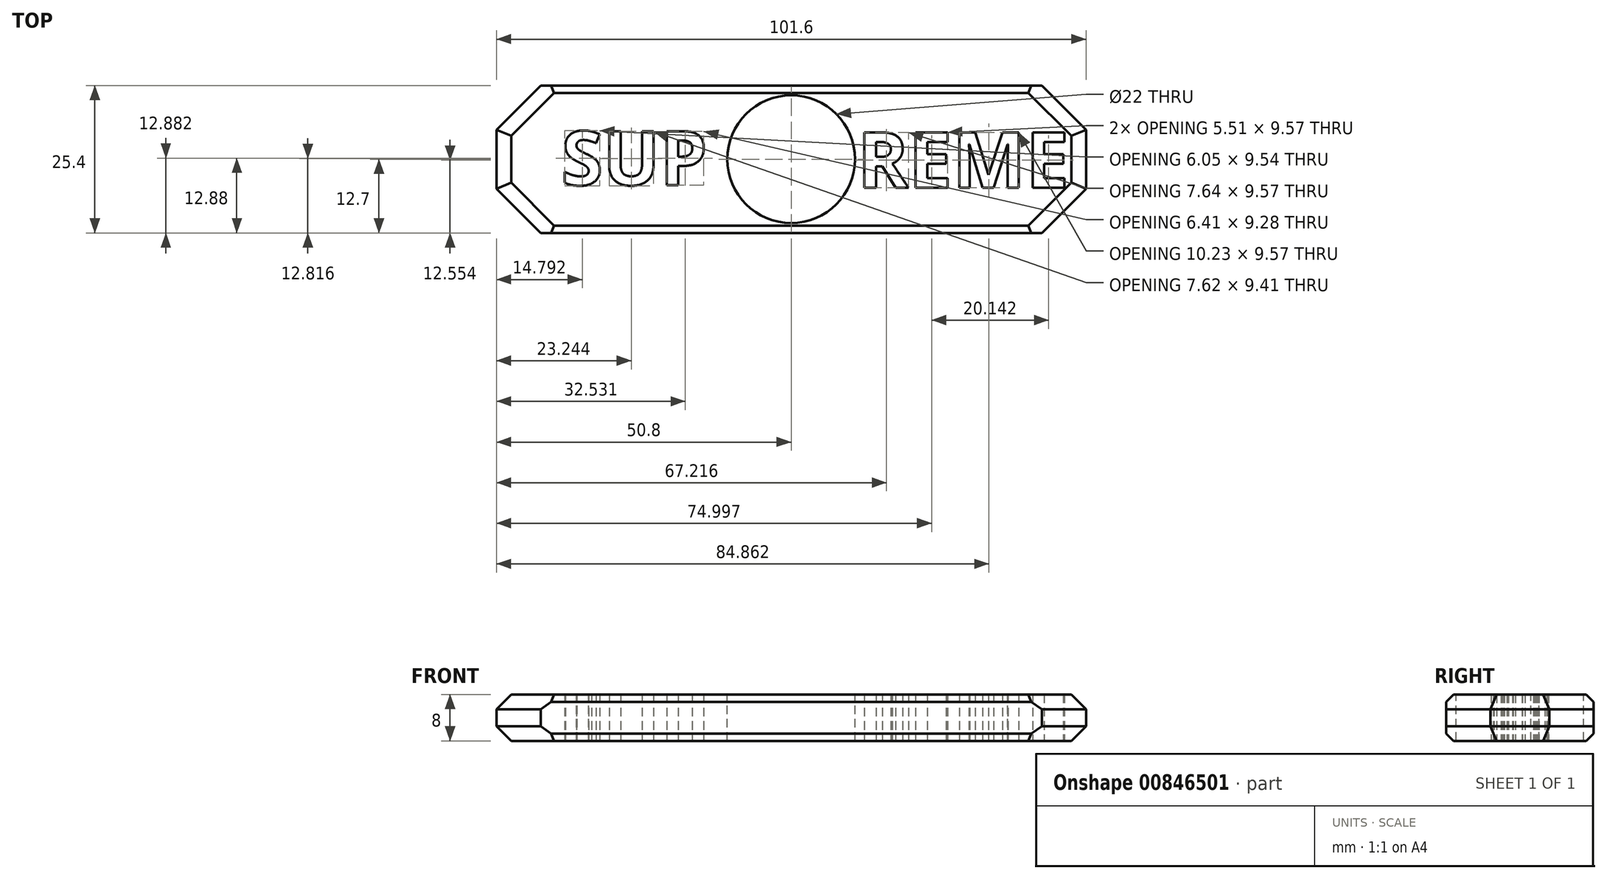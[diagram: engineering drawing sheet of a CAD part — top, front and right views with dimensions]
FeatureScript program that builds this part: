
annotation { "Feature Type Name" : "Feature", "Feature Type Description" : "" }
export const myFeature = defineFeature(function(context is Context, id is Id, definition is map)
    precondition{}
    {
        {
            var Q0;
            Q0=qCreatedBy(makeId("Top.planeOp"),FACE);
            var sketch = newSketch(context, id + "F0", { "sketchPlane" : qUnion([Q0])});
            skLineSegment(sketch, "E0.bottom", {"start": v(-50.8, -12.7) * mm, "end": v(50.8, -12.7) * mm});
            skLineSegment(sketch, "E0.top", {"start": v(-50.8, 12.7) * mm, "end": v(50.8, 12.7) * mm});
            skLineSegment(sketch, "E0.left", {"start": v(-50.8, -12.7) * mm, "end": v(-50.8, 12.7) * mm});
            skLineSegment(sketch, "E0.right", {"start": v(50.8, -12.7) * mm, "end": v(50.8, 12.7) * mm});
            skPoint(sketch, "E0.middle", {"position": v(0, 0) * mm});
            skSolve(sketch);
        }
        {
            var Q0;
            Q0 = qSketchRegion(id + "F0", true);
            extrude(context, id + "F1", {"entities" : qUnion([Q0]), "depth" : 8 * mm, "offsetDistance" : 25.4 * mm});
        }
        {
            var Q0;
            Q0=qCreatedBy(makeId("Top.planeOp"),FACE);
            var sketch = newSketch(context, id + "F2", { "sketchPlane" : qUnion([Q0])});
            skCircle(sketch, "E1", {"center": v(0, 0) * mm, "radius": 11 * mm});
            skSolve(sketch);
        }
        {
            var Q0;
            Q0 = qSketchRegion(id + "F2", true);
            extrude(context, id + "F3", {"entities" : qUnion([Q0]), "operationType" : NewBodyOperationType.REMOVE, "oppositeDirection" : true, "depth" : 25.4 * mm, "offsetDistance" : 25.4 * mm, "hasSecondDirection" : true, "secondDirectionOppositeDirection" : false, "secondDirectionDepth" : 25.4 * mm});
        }
        {
            var Q0;
            Q0=qCreatedBy(makeId("Top.planeOp"),FACE);
            var sketch = newSketch(context, id + "F4", { "sketchPlane" : qUnion([Q0])});
            skText(sketch, "E2", { "text": "SUP\n", "fontName": "OpenSans-Bold.ttf"});
            skText(sketch, "E3", { "text": "REME\n", "fontName": "OpenSans-Bold.ttf"});
            const initialGuessF4  = {"E2": [-0.03963, -0.00446, 1, 0, 0.00936], "E3": [0.01139, -0.00493, 1, 0, 0.00965]};
            skSetInitialGuess(sketch, initialGuessF4);
            skSolve(sketch);
        }
        {
            var Q0;
            Q0 = qSketchRegion(id + "F4", true);
            extrude(context, id + "F5", {"entities" : qUnion([Q0]), "operationType" : NewBodyOperationType.REMOVE, "depth" : 70.36 * mm, "offsetDistance" : 25.4 * mm});
        }
        {
            var Q0;
            Q0=makeQuery(id+"F1.opExtrude","SWEPT_EDGE",EDGE,{"disambiguationData":[OSD([sQuery(id+"F0.wireOp",EDGE,"E0.top"),sQuery(id+"F0.wireOp",EDGE,"E0.left")])]});
            var Q1;
            Q1=makeQuery(id+"F1.opExtrude","SWEPT_EDGE",EDGE,{"disambiguationData":[OSD([sQuery(id+"F0.wireOp",EDGE,"E0.bottom"),sQuery(id+"F0.wireOp",EDGE,"E0.left")])]});
            var Q2;
            Q2=makeQuery(id+"F1.opExtrude","SWEPT_EDGE",EDGE,{"disambiguationData":[OSD([sQuery(id+"F0.wireOp",EDGE,"E0.bottom"),sQuery(id+"F0.wireOp",EDGE,"E0.right")])]});
            var Q3;
            Q3=makeQuery(id+"F1.opExtrude","SWEPT_EDGE",EDGE,{"disambiguationData":[OSD([sQuery(id+"F0.wireOp",EDGE,"E0.top"),sQuery(id+"F0.wireOp",EDGE,"E0.right")])]});
            chamfer(context, id + "F6", {"entities" : qUnion([Q0, Q1, Q2, Q3]), "width" : 7.62 * mm, "tangentPropagation" : true});
        }
        {
            var Q0;
            Q0=makeQuery(id+"F1.opExtrude","CAP_EDGE",EDGE,{"disambiguationData":[OSD([sQuery(id+"F0.wireOp",EDGE,"E0.bottom")])],"isStart":false});
            var Q1;
            Q1=makeQuery(id+"F1.opExtrude","CAP_EDGE",EDGE,{"disambiguationData":[OSD([sQuery(id+"F0.wireOp",EDGE,"E0.top")])],"isStart":false});
            var Q2;
            Q2=makeQuery(id+"F1.opExtrude","CAP_EDGE",EDGE,{"disambiguationData":[OSD([sQuery(id+"F0.wireOp",EDGE,"E0.bottom")])],"isStart":true});
            var Q3;
            Q3=makeQuery(id+"F1.opExtrude","CAP_EDGE",EDGE,{"disambiguationData":[OSD([sQuery(id+"F0.wireOp",EDGE,"E0.top")])],"isStart":true});
            chamfer(context, id + "F7", {"entities" : qUnion([Q0, Q1, Q2, Q3]), "width" : 1.27 * mm, "tangentPropagation" : true});
        }
        {
            var Q0;
            {var subQ0=sQuery(id+"F0.wireOp",EDGE,"E0.right");var subQ1=sQuery(id+"F0.wireOp",EDGE,"E0.left");var subQ2=sQuery(id+"F0.wireOp",EDGE,"E0.top");var subQ3=sQuery(id+"F0.wireOp",EDGE,"E0.bottom");Q0=makeQuery(id+"F6.opChamfer","BLEND_EDGE",EDGE,{"blendedFrom":[makeQuery(id+"F1.opExtrude","SWEPT_EDGE",EDGE,{"disambiguationData":[OSD([subQ3,subQ1])]}),makeQuery(id+"F5.boolean.opBoolean","SPLIT",FACE,{"disambiguationData":[TD([makeQuery(id+"F1.opExtrude","SWEPT_FACE",FACE,{"disambiguationData":[OSD([subQ3])]})])],"derivedFrom":makeQuery(id+"F1.opExtrude","CAP_FACE",FACE,{"disambiguationData":[OSD([subQ3,subQ2,subQ1,subQ0])],"isStart":true})})],"blendedInto":[makeQuery(id+"F5.boolean.opBoolean","SPLIT",FACE,{"disambiguationData":[TD([makeQuery(id+"F1.opExtrude","SWEPT_FACE",FACE,{"disambiguationData":[OSD([subQ3])]})])],"derivedFrom":makeQuery(id+"F1.opExtrude","CAP_FACE",FACE,{"disambiguationData":[OSD([subQ3,subQ2,subQ1,subQ0])],"isStart":true})})]});}
            var Q1;
            Q1=makeQuery(id+"F1.opExtrude","CAP_EDGE",EDGE,{"disambiguationData":[OSD([sQuery(id+"F0.wireOp",EDGE,"E0.left")])],"isStart":true});
            var Q2;
            {var subQ0=sQuery(id+"F0.wireOp",EDGE,"E0.right");var subQ1=sQuery(id+"F0.wireOp",EDGE,"E0.left");var subQ2=sQuery(id+"F0.wireOp",EDGE,"E0.top");var subQ3=sQuery(id+"F0.wireOp",EDGE,"E0.bottom");Q2=makeQuery(id+"F6.opChamfer","BLEND_EDGE",EDGE,{"blendedFrom":[makeQuery(id+"F1.opExtrude","SWEPT_EDGE",EDGE,{"disambiguationData":[OSD([subQ3,subQ1])]}),makeQuery(id+"F5.boolean.opBoolean","SPLIT",FACE,{"disambiguationData":[TD([makeQuery(id+"F1.opExtrude","SWEPT_FACE",FACE,{"disambiguationData":[OSD([subQ3])]})])],"derivedFrom":makeQuery(id+"F1.opExtrude","CAP_FACE",FACE,{"disambiguationData":[OSD([subQ3,subQ2,subQ1,subQ0])],"isStart":false})})],"blendedInto":[makeQuery(id+"F5.boolean.opBoolean","SPLIT",FACE,{"disambiguationData":[TD([makeQuery(id+"F1.opExtrude","SWEPT_FACE",FACE,{"disambiguationData":[OSD([subQ3])]})])],"derivedFrom":makeQuery(id+"F1.opExtrude","CAP_FACE",FACE,{"disambiguationData":[OSD([subQ3,subQ2,subQ1,subQ0])],"isStart":false})})]});}
            var Q3;
            Q3=makeQuery(id+"F1.opExtrude","CAP_EDGE",EDGE,{"disambiguationData":[OSD([sQuery(id+"F0.wireOp",EDGE,"E0.left")])],"isStart":false});
            var Q4;
            {var subQ0=sQuery(id+"F0.wireOp",EDGE,"E0.right");var subQ1=sQuery(id+"F0.wireOp",EDGE,"E0.left");var subQ2=sQuery(id+"F0.wireOp",EDGE,"E0.top");var subQ3=sQuery(id+"F0.wireOp",EDGE,"E0.bottom");Q4=makeQuery(id+"F6.opChamfer","BLEND_EDGE",EDGE,{"blendedFrom":[makeQuery(id+"F1.opExtrude","SWEPT_EDGE",EDGE,{"disambiguationData":[OSD([subQ2,subQ1])]}),makeQuery(id+"F5.boolean.opBoolean","SPLIT",FACE,{"disambiguationData":[TD([makeQuery(id+"F1.opExtrude","SWEPT_FACE",FACE,{"disambiguationData":[OSD([subQ3])]})])],"derivedFrom":makeQuery(id+"F1.opExtrude","CAP_FACE",FACE,{"disambiguationData":[OSD([subQ3,subQ2,subQ1,subQ0])],"isStart":false})})],"blendedInto":[makeQuery(id+"F5.boolean.opBoolean","SPLIT",FACE,{"disambiguationData":[TD([makeQuery(id+"F1.opExtrude","SWEPT_FACE",FACE,{"disambiguationData":[OSD([subQ3])]})])],"derivedFrom":makeQuery(id+"F1.opExtrude","CAP_FACE",FACE,{"disambiguationData":[OSD([subQ3,subQ2,subQ1,subQ0])],"isStart":false})})]});}
            var Q5;
            {var subQ0=sQuery(id+"F0.wireOp",EDGE,"E0.right");var subQ1=sQuery(id+"F0.wireOp",EDGE,"E0.left");var subQ2=sQuery(id+"F0.wireOp",EDGE,"E0.top");var subQ3=sQuery(id+"F0.wireOp",EDGE,"E0.bottom");Q5=makeQuery(id+"F6.opChamfer","BLEND_EDGE",EDGE,{"blendedFrom":[makeQuery(id+"F1.opExtrude","SWEPT_EDGE",EDGE,{"disambiguationData":[OSD([subQ2,subQ1])]}),makeQuery(id+"F5.boolean.opBoolean","SPLIT",FACE,{"disambiguationData":[TD([makeQuery(id+"F1.opExtrude","SWEPT_FACE",FACE,{"disambiguationData":[OSD([subQ3])]})])],"derivedFrom":makeQuery(id+"F1.opExtrude","CAP_FACE",FACE,{"disambiguationData":[OSD([subQ3,subQ2,subQ1,subQ0])],"isStart":true})})],"blendedInto":[makeQuery(id+"F5.boolean.opBoolean","SPLIT",FACE,{"disambiguationData":[TD([makeQuery(id+"F1.opExtrude","SWEPT_FACE",FACE,{"disambiguationData":[OSD([subQ3])]})])],"derivedFrom":makeQuery(id+"F1.opExtrude","CAP_FACE",FACE,{"disambiguationData":[OSD([subQ3,subQ2,subQ1,subQ0])],"isStart":true})})]});}
            var Q6;
            {var subQ0=sQuery(id+"F0.wireOp",EDGE,"E0.right");var subQ1=sQuery(id+"F0.wireOp",EDGE,"E0.left");var subQ2=sQuery(id+"F0.wireOp",EDGE,"E0.top");var subQ3=sQuery(id+"F0.wireOp",EDGE,"E0.bottom");Q6=makeQuery(id+"F6.opChamfer","BLEND_EDGE",EDGE,{"blendedFrom":[makeQuery(id+"F1.opExtrude","SWEPT_EDGE",EDGE,{"disambiguationData":[OSD([subQ2,subQ0])]}),makeQuery(id+"F5.boolean.opBoolean","SPLIT",FACE,{"disambiguationData":[TD([makeQuery(id+"F1.opExtrude","SWEPT_FACE",FACE,{"disambiguationData":[OSD([subQ3])]})])],"derivedFrom":makeQuery(id+"F1.opExtrude","CAP_FACE",FACE,{"disambiguationData":[OSD([subQ3,subQ2,subQ1,subQ0])],"isStart":false})})],"blendedInto":[makeQuery(id+"F5.boolean.opBoolean","SPLIT",FACE,{"disambiguationData":[TD([makeQuery(id+"F1.opExtrude","SWEPT_FACE",FACE,{"disambiguationData":[OSD([subQ3])]})])],"derivedFrom":makeQuery(id+"F1.opExtrude","CAP_FACE",FACE,{"disambiguationData":[OSD([subQ3,subQ2,subQ1,subQ0])],"isStart":false})})]});}
            var Q7;
            Q7=makeQuery(id+"F1.opExtrude","CAP_EDGE",EDGE,{"disambiguationData":[OSD([sQuery(id+"F0.wireOp",EDGE,"E0.right")])],"isStart":false});
            var Q8;
            {var subQ0=sQuery(id+"F0.wireOp",EDGE,"E0.right");var subQ1=sQuery(id+"F0.wireOp",EDGE,"E0.left");var subQ2=sQuery(id+"F0.wireOp",EDGE,"E0.top");var subQ3=sQuery(id+"F0.wireOp",EDGE,"E0.bottom");Q8=makeQuery(id+"F6.opChamfer","BLEND_EDGE",EDGE,{"blendedFrom":[makeQuery(id+"F1.opExtrude","SWEPT_EDGE",EDGE,{"disambiguationData":[OSD([subQ3,subQ0])]}),makeQuery(id+"F5.boolean.opBoolean","SPLIT",FACE,{"disambiguationData":[TD([makeQuery(id+"F1.opExtrude","SWEPT_FACE",FACE,{"disambiguationData":[OSD([subQ3])]})])],"derivedFrom":makeQuery(id+"F1.opExtrude","CAP_FACE",FACE,{"disambiguationData":[OSD([subQ3,subQ2,subQ1,subQ0])],"isStart":false})})],"blendedInto":[makeQuery(id+"F5.boolean.opBoolean","SPLIT",FACE,{"disambiguationData":[TD([makeQuery(id+"F1.opExtrude","SWEPT_FACE",FACE,{"disambiguationData":[OSD([subQ3])]})])],"derivedFrom":makeQuery(id+"F1.opExtrude","CAP_FACE",FACE,{"disambiguationData":[OSD([subQ3,subQ2,subQ1,subQ0])],"isStart":false})})]});}
            var Q9;
            {var subQ0=sQuery(id+"F0.wireOp",EDGE,"E0.right");var subQ1=sQuery(id+"F0.wireOp",EDGE,"E0.left");var subQ2=sQuery(id+"F0.wireOp",EDGE,"E0.top");var subQ3=sQuery(id+"F0.wireOp",EDGE,"E0.bottom");Q9=makeQuery(id+"F6.opChamfer","BLEND_EDGE",EDGE,{"blendedFrom":[makeQuery(id+"F1.opExtrude","SWEPT_EDGE",EDGE,{"disambiguationData":[OSD([subQ3,subQ0])]}),makeQuery(id+"F5.boolean.opBoolean","SPLIT",FACE,{"disambiguationData":[TD([makeQuery(id+"F1.opExtrude","SWEPT_FACE",FACE,{"disambiguationData":[OSD([subQ3])]})])],"derivedFrom":makeQuery(id+"F1.opExtrude","CAP_FACE",FACE,{"disambiguationData":[OSD([subQ3,subQ2,subQ1,subQ0])],"isStart":true})})],"blendedInto":[makeQuery(id+"F5.boolean.opBoolean","SPLIT",FACE,{"disambiguationData":[TD([makeQuery(id+"F1.opExtrude","SWEPT_FACE",FACE,{"disambiguationData":[OSD([subQ3])]})])],"derivedFrom":makeQuery(id+"F1.opExtrude","CAP_FACE",FACE,{"disambiguationData":[OSD([subQ3,subQ2,subQ1,subQ0])],"isStart":true})})]});}
            var Q10;
            Q10=makeQuery(id+"F1.opExtrude","CAP_EDGE",EDGE,{"disambiguationData":[OSD([sQuery(id+"F0.wireOp",EDGE,"E0.right")])],"isStart":true});
            var Q11;
            {var subQ0=sQuery(id+"F0.wireOp",EDGE,"E0.right");var subQ1=sQuery(id+"F0.wireOp",EDGE,"E0.left");var subQ2=sQuery(id+"F0.wireOp",EDGE,"E0.top");var subQ3=sQuery(id+"F0.wireOp",EDGE,"E0.bottom");Q11=makeQuery(id+"F6.opChamfer","BLEND_EDGE",EDGE,{"blendedFrom":[makeQuery(id+"F1.opExtrude","SWEPT_EDGE",EDGE,{"disambiguationData":[OSD([subQ2,subQ0])]}),makeQuery(id+"F5.boolean.opBoolean","SPLIT",FACE,{"disambiguationData":[TD([makeQuery(id+"F1.opExtrude","SWEPT_FACE",FACE,{"disambiguationData":[OSD([subQ3])]})])],"derivedFrom":makeQuery(id+"F1.opExtrude","CAP_FACE",FACE,{"disambiguationData":[OSD([subQ3,subQ2,subQ1,subQ0])],"isStart":true})})],"blendedInto":[makeQuery(id+"F5.boolean.opBoolean","SPLIT",FACE,{"disambiguationData":[TD([makeQuery(id+"F1.opExtrude","SWEPT_FACE",FACE,{"disambiguationData":[OSD([subQ3])]})])],"derivedFrom":makeQuery(id+"F1.opExtrude","CAP_FACE",FACE,{"disambiguationData":[OSD([subQ3,subQ2,subQ1,subQ0])],"isStart":true})})]});}
            chamfer(context, id + "F8", {"entities" : qUnion([Q0, Q1, Q2, Q3, Q4, Q5, Q6, Q7, Q8, Q9, Q10, Q11]), "width" : 2.54 * mm, "tangentPropagation" : true});
        }
    });
